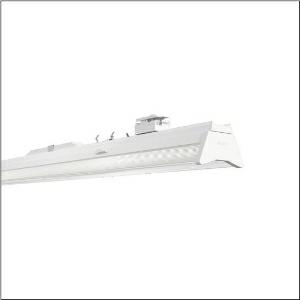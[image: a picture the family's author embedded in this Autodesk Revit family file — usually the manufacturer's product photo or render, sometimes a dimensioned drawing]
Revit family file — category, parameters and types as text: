
# Revit family: licross_r__11_performance_mo_51td16mn4axg_aad5
name_source: partatom
category: Lighting Fixtures
units: mm (PartAtom-declared; Revit-internal decimal feet)

## family parameters
Cut with Voids When Loaded = No
Host = Face
Light Source = No
Part Type = Normal
Room Calculation Point = No
Round Connector Dimension = Use Diameter
Shared = No

## types (1)
- --- (1 x LED, 10160 lm, 55.3 W, 4000K)
    Apparent Load = 55 VA
    CIE Flux Codes = 66 88 96 79 100
    Color Rendering = 80
    Color Temperature = 4000K
    Default Elevation = 1800 mm
    Description = Licross® 11 Performance MO, luminaire insert, of sheet steel, galvanised, coil coated, white, length: 1.500mm, width: 120mm, height: 123mm, LED rated luminous flux: 10.160lm, light colour: 840, control gear: ON/OFF Multilumen, with plug, 3-pole, with phase selection, mains connection: 220..240V, AC, 50/60Hz, rated input power: 55W, internal wiring halogen-free, primary light control with lens, of plastic, primary optical cover: cover, of PMMA, light emission: direct/indirect distribution, primary light characteristic: symmetric, protection rating (complete): IP54, insulation class (complete): insulation class I (protective earthing), certification: CE, ENEC, VDE, UKCA, protection symbol: D if used in an environment with non-conductive dust loads with corresponding accessories, impact resistance: IK06, permissible ambient temperature for indoor applications: -35..+40°C, corresponds to IFS (International Featured Standards) requirements for safety and quality in the food industry, reducing of maximum allowable ambient temperature of 5°C with ceiling mounting, LABS conformity tested according to VDMA 24364:2018-05, packaging unit: 1 piece
    Height = 114 mm
    Lamp = 1 x LED
    Lamp Light Flux = 10160 lm
    Lamp Power = 55.3 W
    Lamp count = 1
    Length = 1500 mm
    Luminous efficacy = 184 lm/W
    Manufacturer = Siteco
    ModVariant = No
    Model = 51TD16MN4AXG
    Mounting Place = Ceiling
    Mounting Type = Pendant
    Number of Poles = 1
    OnlyDefault = Yes
    Power Factor = 1
    Product Name = Licross® 11 Performance MO
    Product group = luminaire insert | ceiling pendant
    ProductGroupID = 902
    Protection Class = Protection class I
    Protection Degree = IP 54
    RLX_Detail_Level = 1
    RLX_Emergency_Light_Flux = 0 lm
    RLX_Emergency_Type = 0
    RLX_Emergency_Type_DB = No
    RlxData = <blob elided: 31861 chars, md5=5a76fdb5>
    Socket = socket
    Standby Power = 0 W
    System Light Flux = 10160 lm
    System Power = 55 W
    Type Comments = factory setting: luminous flux: 100 % | (A | C | E) | 126 mA
    Type Image = l_1256138.jpg
    URL = http://relux.com
    VarID = @adj_107621
    Voltage = 0 V
    Weight = 0.00 kg
    Width = 120 mm

## geometry (parser evidence)
native form markers: Blend x4, Sweep x13
no freeform markers — native parametric forms only
